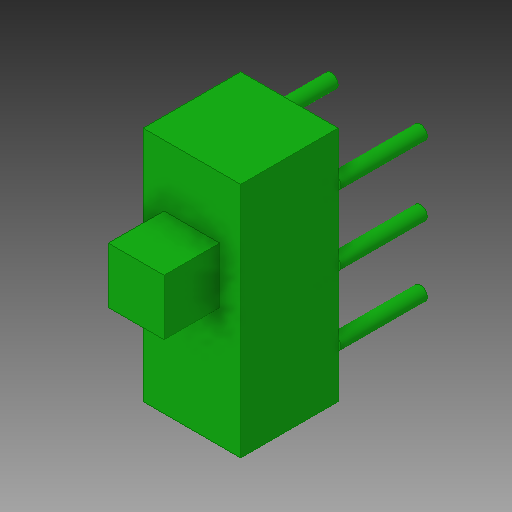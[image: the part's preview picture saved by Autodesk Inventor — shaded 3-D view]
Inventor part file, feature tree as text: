
AUTODESK INVENTOR PART (.ipt)
format: ipt  version: 2018.1 (Build 221171000, 171)  size: 130,560 bytes
history: native  units: mm
features: extrude x3, sketch x3, other x1, pattern_linear x1
ambient origin geometry x8: Origin, YZ Plane, XZ Plane, XY Plane, X Axis, Y Axis, Z Axis, Center Point
bodies: Body1 (feature_tree)
feature tree (8):
  other  "ソリッド1"
  extrude  "押し出し1"  Depth=3.5mm
  extrude  "押し出し2"  Depth=8.5mm
  pattern_linear  "矩形状パターン1"  Spacing1=3.5mm  [1 undecoded]
  extrude  "押し出し3"  Depth=3.2mm
  sketch  "スケッチ1"
  sketch  "スケッチ2"
  sketch  "スケッチ3"
note: 1 required parameter value undecoded (feature->parameter linkage not recoverable at this tier; creation-order binding heuristic only, values carry confidence <= 0.55)
